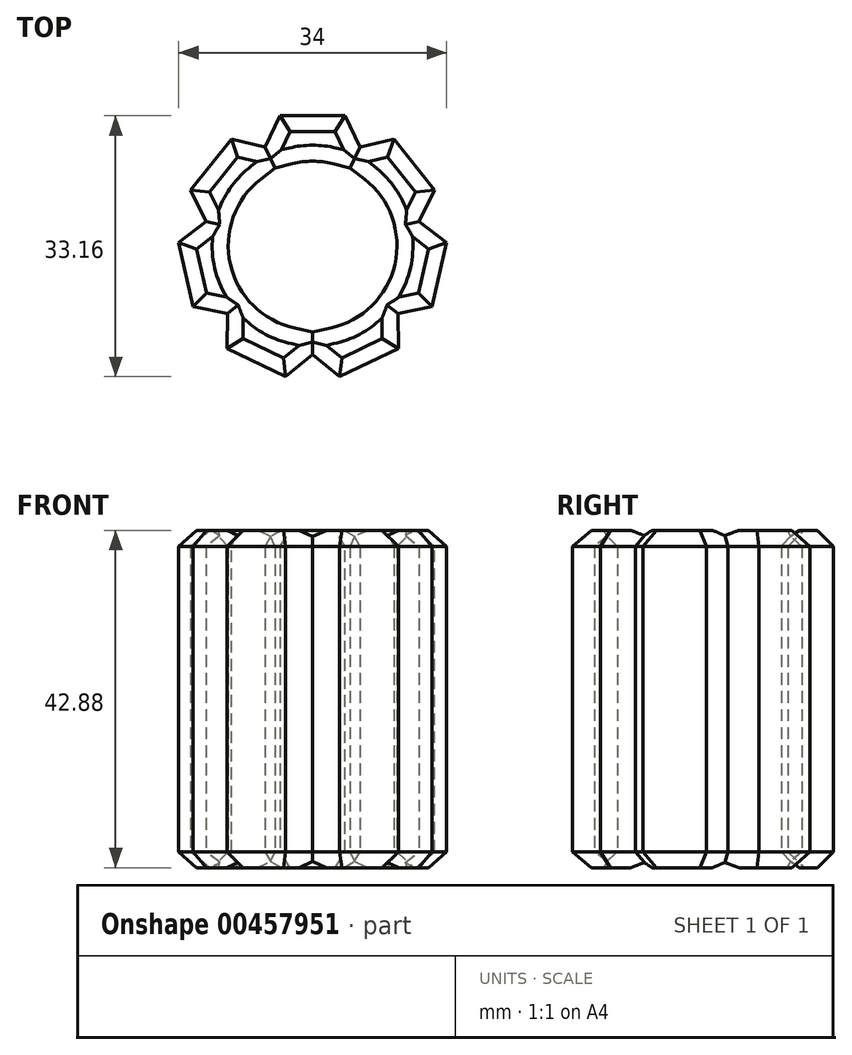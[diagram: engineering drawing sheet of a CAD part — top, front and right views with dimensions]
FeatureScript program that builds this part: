
annotation { "Feature Type Name" : "Feature", "Feature Type Description" : "" }
export const myFeature = defineFeature(function(context is Context, id is Id, definition is map)
    precondition{}
    {
        {
            var Q0;
            Q0=qCreatedBy(makeId("Top.planeOp"),FACE);
            var sketch = newSketch(context, id + "F0", { "sketchPlane" : qUnion([Q0])});
            skCircle(sketch, "E0", {"center": v(0, 0) * mm, "radius": 10.72 * mm});
            skLineSegment(sketch, "E1", {"start": v(0, 0) * mm, "end": v(0, 25.4) * mm, "construction": true});
            skPoint(sketch, "E2.center", {"position": v(-0.83, 0) * mm});
            skLineSegment(sketch, "E3", {"start": v(0, 25.4) * mm, "end": v(-11.82, 0) * mm});
            skLineSegment(sketch, "E4", {"start": v(0, 25.4) * mm, "end": v(11.82, 0) * mm});
            skLineSegment(sketch, "E5.1.0", {"start": v(-19.86, 15.84) * mm, "end": v(7.37, 9.24) * mm});
            skLineSegment(sketch, "E5.1.1", {"start": v(-19.86, 15.84) * mm, "end": v(-7.37, -9.24) * mm});
            skLineSegment(sketch, "E5.2.0", {"start": v(-24.76, -5.65) * mm, "end": v(-2.63, 11.53) * mm});
            skLineSegment(sketch, "E5.2.1", {"start": v(-24.76, -5.65) * mm, "end": v(2.63, -11.53) * mm});
            skLineSegment(sketch, "E5.3.0", {"start": v(-11.02, -22.88) * mm, "end": v(-10.65, 5.13) * mm});
            skLineSegment(sketch, "E5.3.1", {"start": v(-11.02, -22.88) * mm, "end": v(10.65, -5.13) * mm});
            skCircle(sketch, "E6", {"center": v(0, 0) * mm, "radius": 25.4 * mm});
            skLineSegment(sketch, "E7.2.4.0", {"start": v(11.02, -22.88) * mm, "end": v(-10.65, -5.13) * mm});
            skLineSegment(sketch, "E7.3.4.0", {"start": v(11.02, -22.88) * mm, "end": v(10.65, 5.13) * mm});
            skLineSegment(sketch, "E7.2.5.0", {"start": v(24.76, -5.65) * mm, "end": v(-2.63, -11.53) * mm});
            skLineSegment(sketch, "E7.3.5.0", {"start": v(24.76, -5.65) * mm, "end": v(2.63, 11.53) * mm});
            skLineSegment(sketch, "E7.2.6.0", {"start": v(19.86, 15.84) * mm, "end": v(7.37, -9.24) * mm});
            skLineSegment(sketch, "E7.3.6.0", {"start": v(19.86, 15.84) * mm, "end": v(-7.37, 9.24) * mm});
            skSolve(sketch);
        }
        {
            var Q0;
            {var subQ1=sQuery(id+"F0.wireOp",EDGE,"E3");var subQ7=sQuery(id+"F0.wireOp",EDGE,"E4");var subQ8=makeQuery(id+"F0.imprint","INTERSECT",VERTEX,{"derivedFrom":[subQ1,subQ7]});Q0=makeQuery(id+"F0.imprint","IMPRINT",FACE,{"disambiguationData":[TD([[makeQuery(id+"F0.imprint","IMPRINT",EDGE,{"disambiguationData":[TD([[subQ8,-1.0]])],"derivedFrom":subQ1}),1.0]])]});}
            var Q1;
            {var subQ1=sQuery(id+"F0.wireOp",EDGE,"E5.1.0");var subQ5=sQuery(id+"F0.wireOp",EDGE,"E3");var subQ10=makeQuery(id+"F0.imprint","INTERSECT",VERTEX,{"derivedFrom":[subQ5,subQ1]});Q1=makeQuery(id+"F0.imprint","IMPRINT",FACE,{"disambiguationData":[TD([[makeQuery(id+"F0.imprint","IMPRINT",EDGE,{"disambiguationData":[TD([[subQ10,-1.0]])],"derivedFrom":subQ5}),-1.0]])]});}
            var Q2;
            {var subQ1=sQuery(id+"F0.wireOp",EDGE,"E4");var subQ8=sQuery(id+"F0.wireOp",EDGE,"E5.3.1");var subQ9=makeQuery(id+"F0.imprint","INTERSECT",VERTEX,{"derivedFrom":[subQ1,subQ8]});Q2=makeQuery(id+"F0.imprint","IMPRINT",FACE,{"disambiguationData":[TD([[makeQuery(id+"F0.imprint","IMPRINT",EDGE,{"disambiguationData":[TD([[subQ9,-1.0]])],"derivedFrom":subQ1}),1.0]])]});}
            var Q3;
            {var subQ1=sQuery(id+"F0.wireOp",EDGE,"E5.2.0");var subQ3=sQuery(id+"F0.wireOp",EDGE,"E5.1.1");var subQ4=makeQuery(id+"F0.imprint","INTERSECT",VERTEX,{"derivedFrom":[subQ3,subQ1]});Q3=makeQuery(id+"F0.imprint","IMPRINT",FACE,{"disambiguationData":[TD([[makeQuery(id+"F0.imprint","IMPRINT",EDGE,{"disambiguationData":[TD([[subQ4,-1.0]])],"derivedFrom":subQ3}),-1.0]])]});}
            var Q4;
            {var subQ0=sQuery(id+"F0.wireOp",EDGE,"E5.3.0");var subQ1=sQuery(id+"F0.wireOp",EDGE,"E0");var subQ2=makeQuery(id+"F0.imprint","INTERSECT",VERTEX,{"derivedFrom":[subQ1,subQ0]});Q4=makeQuery(id+"F0.imprint","IMPRINT",FACE,{"disambiguationData":[TD([[makeQuery(id+"F0.imprint","IMPRINT",EDGE,{"disambiguationData":[TD([[subQ2,-1.0]])],"derivedFrom":subQ1}),-1.0]])]});}
            var Q5;
            {var subQ0=sQuery(id+"F0.wireOp",EDGE,"E5.2.0");var subQ1=sQuery(id+"F0.wireOp",EDGE,"E0");var subQ2=makeQuery(id+"F0.imprint","INTERSECT",VERTEX,{"derivedFrom":[subQ1,subQ0]});Q5=makeQuery(id+"F0.imprint","IMPRINT",FACE,{"disambiguationData":[TD([[makeQuery(id+"F0.imprint","IMPRINT",EDGE,{"disambiguationData":[TD([[subQ2,-1.0]])],"derivedFrom":subQ1}),-1.0]])]});}
            var Q6;
            {var subQ0=sQuery(id+"F0.wireOp",EDGE,"E5.1.0");var subQ1=sQuery(id+"F0.wireOp",EDGE,"E0");var subQ2=makeQuery(id+"F0.imprint","INTERSECT",VERTEX,{"derivedFrom":[subQ1,subQ0]});Q6=makeQuery(id+"F0.imprint","IMPRINT",FACE,{"disambiguationData":[TD([[makeQuery(id+"F0.imprint","IMPRINT",EDGE,{"disambiguationData":[TD([[subQ2,-1.0]])],"derivedFrom":subQ1}),-1.0]])]});}
            var Q7;
            {var subQ0=sQuery(id+"F0.wireOp",EDGE,"E5.3.1");var subQ1=sQuery(id+"F0.wireOp",EDGE,"E0");var subQ2=makeQuery(id+"F0.imprint","INTERSECT",VERTEX,{"derivedFrom":[subQ1,subQ0]});Q7=makeQuery(id+"F0.imprint","IMPRINT",FACE,{"disambiguationData":[TD([[makeQuery(id+"F0.imprint","IMPRINT",EDGE,{"disambiguationData":[TD([[subQ2,1.0]])],"derivedFrom":subQ1}),-1.0]])]});}
            var Q8;
            {var subQ0=sQuery(id+"F0.wireOp",EDGE,"E4");var subQ1=sQuery(id+"F0.wireOp",EDGE,"E0");var subQ2=makeQuery(id+"F0.imprint","INTERSECT",VERTEX,{"derivedFrom":[subQ1,subQ0]});Q8=makeQuery(id+"F0.imprint","IMPRINT",FACE,{"disambiguationData":[TD([[makeQuery(id+"F0.imprint","IMPRINT",EDGE,{"disambiguationData":[TD([[subQ2,1.0]])],"derivedFrom":subQ1}),-1.0]])]});}
            var Q9;
            {var subQ0=sQuery(id+"F0.wireOp",EDGE,"E5.1.1");var subQ1=sQuery(id+"F0.wireOp",EDGE,"E0");var subQ2=makeQuery(id+"F0.imprint","INTERSECT",VERTEX,{"derivedFrom":[subQ1,subQ0]});Q9=makeQuery(id+"F0.imprint","IMPRINT",FACE,{"disambiguationData":[TD([[makeQuery(id+"F0.imprint","IMPRINT",EDGE,{"disambiguationData":[TD([[subQ2,-1.0]])],"derivedFrom":subQ1}),-1.0]])]});}
            var Q10;
            {var subQ0=sQuery(id+"F0.wireOp",EDGE,"E3");var subQ1=sQuery(id+"F0.wireOp",EDGE,"E0");var subQ2=makeQuery(id+"F0.imprint","INTERSECT",VERTEX,{"derivedFrom":[subQ1,subQ0]});Q10=makeQuery(id+"F0.imprint","IMPRINT",FACE,{"disambiguationData":[TD([[makeQuery(id+"F0.imprint","IMPRINT",EDGE,{"disambiguationData":[TD([[subQ2,-1.0]])],"derivedFrom":subQ1}),-1.0]])]});}
            var Q11;
            {var subQ0=sQuery(id+"F0.wireOp",EDGE,"E5.3.1");var subQ1=sQuery(id+"F0.wireOp",EDGE,"E0");var subQ2=makeQuery(id+"F0.imprint","INTERSECT",VERTEX,{"derivedFrom":[subQ1,subQ0]});Q11=makeQuery(id+"F0.imprint","IMPRINT",FACE,{"disambiguationData":[TD([[makeQuery(id+"F0.imprint","IMPRINT",EDGE,{"disambiguationData":[TD([[subQ2,-1.0]])],"derivedFrom":subQ1}),-1.0]])]});}
            var Q12;
            {var subQ0=sQuery(id+"F0.wireOp",EDGE,"E7.2.5.0");var subQ1=sQuery(id+"F0.wireOp",EDGE,"E7.3.4.0");var subQ2=makeQuery(id+"F0.imprint","INTERSECT",VERTEX,{"derivedFrom":[subQ1,subQ0]});Q12=makeQuery(id+"F0.imprint","IMPRINT",FACE,{"disambiguationData":[TD([[makeQuery(id+"F0.imprint","IMPRINT",EDGE,{"disambiguationData":[TD([[subQ2,-1.0]])],"derivedFrom":subQ1}),-1.0]])]});}
            var Q13;
            {var subQ0=sQuery(id+"F0.wireOp",EDGE,"E7.2.4.0");var subQ1=sQuery(id+"F0.wireOp",EDGE,"E5.3.1");var subQ2=makeQuery(id+"F0.imprint","INTERSECT",VERTEX,{"derivedFrom":[subQ1,subQ0]});Q13=makeQuery(id+"F0.imprint","IMPRINT",FACE,{"disambiguationData":[TD([[makeQuery(id+"F0.imprint","IMPRINT",EDGE,{"disambiguationData":[TD([[subQ2,-1.0]])],"derivedFrom":subQ1}),-1.0]])]});}
            var Q14;
            {var subQ0=sQuery(id+"F0.wireOp",EDGE,"E5.3.0");var subQ1=sQuery(id+"F0.wireOp",EDGE,"E5.2.1");var subQ2=makeQuery(id+"F0.imprint","INTERSECT",VERTEX,{"derivedFrom":[subQ1,subQ0]});Q14=makeQuery(id+"F0.imprint","IMPRINT",FACE,{"disambiguationData":[TD([[makeQuery(id+"F0.imprint","IMPRINT",EDGE,{"disambiguationData":[TD([[subQ2,-1.0]])],"derivedFrom":subQ1}),-1.0]])]});}
            var Q15;
            {var subQ0=sQuery(id+"F0.wireOp",EDGE,"E7.3.6.0");var subQ1=sQuery(id+"F0.wireOp",EDGE,"E4");var subQ2=makeQuery(id+"F0.imprint","INTERSECT",VERTEX,{"derivedFrom":[subQ1,subQ0]});Q15=makeQuery(id+"F0.imprint","IMPRINT",FACE,{"disambiguationData":[TD([[makeQuery(id+"F0.imprint","IMPRINT",EDGE,{"disambiguationData":[TD([[subQ2,-1.0]])],"derivedFrom":subQ1}),1.0]])]});}
            var Q16;
            {var subQ3=sQuery(id+"F0.wireOp",EDGE,"E4");var subQ8=sQuery(id+"F0.wireOp",EDGE,"E7.3.6.0");var subQ10=makeQuery(id+"F0.imprint","INTERSECT",VERTEX,{"derivedFrom":[subQ3,subQ8]});Q16=makeQuery(id+"F0.imprint","IMPRINT",FACE,{"disambiguationData":[TD([[makeQuery(id+"F0.imprint","IMPRINT",EDGE,{"disambiguationData":[TD([[subQ10,-1.0]])],"derivedFrom":subQ3}),-1.0]])]});}
            var Q17;
            {var subQ1=sQuery(id+"F0.wireOp",EDGE,"E5.3.1");var subQ8=sQuery(id+"F0.wireOp",EDGE,"E0");var subQ9=makeQuery(id+"F0.imprint","INTERSECT",VERTEX,{"derivedFrom":[subQ8,subQ1]});Q17=makeQuery(id+"F0.imprint","IMPRINT",FACE,{"disambiguationData":[TD([[makeQuery(id+"F0.imprint","IMPRINT",EDGE,{"disambiguationData":[TD([[subQ9,1.0]])],"derivedFrom":subQ1}),-1.0]])]});}
            var Q18;
            {var subQ1=sQuery(id+"F0.wireOp",EDGE,"E5.2.1");var subQ8=sQuery(id+"F0.wireOp",EDGE,"E0");var subQ9=makeQuery(id+"F0.imprint","INTERSECT",VERTEX,{"derivedFrom":[subQ8,subQ1]});Q18=makeQuery(id+"F0.imprint","IMPRINT",FACE,{"disambiguationData":[TD([[makeQuery(id+"F0.imprint","IMPRINT",EDGE,{"disambiguationData":[TD([[subQ9,1.0]])],"derivedFrom":subQ1}),-1.0]])]});}
            var Q19;
            {var subQ0=sQuery(id+"F0.wireOp",EDGE,"E4");var subQ1=sQuery(id+"F0.wireOp",EDGE,"E0");var subQ2=makeQuery(id+"F0.imprint","INTERSECT",VERTEX,{"derivedFrom":[subQ1,subQ0]});Q19=makeQuery(id+"F0.imprint","IMPRINT",FACE,{"disambiguationData":[TD([[makeQuery(id+"F0.imprint","IMPRINT",EDGE,{"disambiguationData":[TD([[subQ2,-1.0]])],"derivedFrom":subQ1}),-1.0]])]});}
            var Q20;
            {var subQ0=sQuery(id+"F0.wireOp",EDGE,"E7.3.4.0");var subQ1=sQuery(id+"F0.wireOp",EDGE,"E0");var subQ2=makeQuery(id+"F0.imprint","INTERSECT",VERTEX,{"derivedFrom":[subQ1,subQ0]});Q20=makeQuery(id+"F0.imprint","IMPRINT",FACE,{"disambiguationData":[TD([[makeQuery(id+"F0.imprint","IMPRINT",EDGE,{"disambiguationData":[TD([[subQ2,1.0]])],"derivedFrom":subQ1}),-1.0]])]});}
            var Q21;
            {var subQ3=sQuery(id+"F0.wireOp",EDGE,"E3");var subQ8=sQuery(id+"F0.wireOp",EDGE,"E5.1.0");var subQ9=makeQuery(id+"F0.imprint","INTERSECT",VERTEX,{"derivedFrom":[subQ3,subQ8]});Q21=makeQuery(id+"F0.imprint","IMPRINT",FACE,{"disambiguationData":[TD([[makeQuery(id+"F0.imprint","IMPRINT",EDGE,{"disambiguationData":[TD([[subQ9,-1.0]])],"derivedFrom":subQ3}),1.0]])]});}
            var Q22;
            {var subQ5=sQuery(id+"F0.wireOp",EDGE,"E3");var subQ6=sQuery(id+"F0.wireOp",EDGE,"E0");var subQ7=makeQuery(id+"F0.imprint","INTERSECT",VERTEX,{"derivedFrom":[subQ6,subQ5]});Q22=makeQuery(id+"F0.imprint","IMPRINT",FACE,{"disambiguationData":[TD([[makeQuery(id+"F0.imprint","IMPRINT",EDGE,{"disambiguationData":[TD([[subQ7,1.0]])],"derivedFrom":subQ5}),-1.0]])]});}
            var Q23;
            {var subQ5=sQuery(id+"F0.wireOp",EDGE,"E5.1.1");var subQ7=sQuery(id+"F0.wireOp",EDGE,"E0");var subQ8=makeQuery(id+"F0.imprint","INTERSECT",VERTEX,{"derivedFrom":[subQ7,subQ5]});Q23=makeQuery(id+"F0.imprint","IMPRINT",FACE,{"disambiguationData":[TD([[makeQuery(id+"F0.imprint","IMPRINT",EDGE,{"disambiguationData":[TD([[subQ8,1.0]])],"derivedFrom":subQ5}),-1.0]])]});}
            var Q24;
            {var subQ0=sQuery(id+"F0.wireOp",EDGE,"E7.2.4.0");var subQ1=sQuery(id+"F0.wireOp",EDGE,"E0");var subQ2=makeQuery(id+"F0.imprint","INTERSECT",VERTEX,{"derivedFrom":[subQ1,subQ0]});Q24=makeQuery(id+"F0.imprint","IMPRINT",FACE,{"disambiguationData":[TD([[makeQuery(id+"F0.imprint","IMPRINT",EDGE,{"disambiguationData":[TD([[subQ2,-1.0]])],"derivedFrom":subQ1}),-1.0]])]});}
            extrude(context, id + "F1", {"entities" : qUnion([Q0, Q1, Q2, Q3, Q4, Q5, Q6, Q7, Q8, Q9, Q10, Q11, Q12, Q13, Q14, Q15, Q16, Q17, Q18, Q19, Q20, Q21, Q22, Q23, Q24]), "endBound" : BoundingType.SYMMETRIC, "depth" : 42.88 * mm, "offsetDistance" : 25.4 * mm});
        }
        {
            var Q0;
            Q0=makeQuery(id+"F1.opExtrude","SWEPT_EDGE",EDGE,{"disambiguationData":[OSD([sQuery(id+"F0.wireOp",EDGE,"E6"),sQuery(id+"F0.wireOp",EDGE,"E7.2.5.0"),sQuery(id+"F0.wireOp",EDGE,"E7.3.5.0")])]});
            var Q1;
            Q1=makeQuery(id+"F1.opExtrude","SWEPT_EDGE",EDGE,{"disambiguationData":[OSD([sQuery(id+"F0.wireOp",EDGE,"E6"),sQuery(id+"F0.wireOp",EDGE,"E7.2.6.0"),sQuery(id+"F0.wireOp",EDGE,"E7.3.6.0")])]});
            var Q2;
            Q2=makeQuery(id+"F1.opExtrude","SWEPT_EDGE",EDGE,{"disambiguationData":[OSD([sQuery(id+"F0.wireOp",EDGE,"E5.1.0"),sQuery(id+"F0.wireOp",EDGE,"E5.1.1"),sQuery(id+"F0.wireOp",EDGE,"E6")])]});
            var Q3;
            Q3=makeQuery(id+"F1.opExtrude","SWEPT_EDGE",EDGE,{"disambiguationData":[OSD([sQuery(id+"F0.wireOp",EDGE,"E5.2.0"),sQuery(id+"F0.wireOp",EDGE,"E5.2.1"),sQuery(id+"F0.wireOp",EDGE,"E6")])]});
            var Q4;
            Q4=makeQuery(id+"F1.opExtrude","SWEPT_EDGE",EDGE,{"disambiguationData":[OSD([sQuery(id+"F0.wireOp",EDGE,"E5.3.0"),sQuery(id+"F0.wireOp",EDGE,"E5.3.1"),sQuery(id+"F0.wireOp",EDGE,"E6")])]});
            var Q5;
            Q5=makeQuery(id+"F1.opExtrude","SWEPT_EDGE",EDGE,{"disambiguationData":[OSD([sQuery(id+"F0.wireOp",EDGE,"E6"),sQuery(id+"F0.wireOp",EDGE,"E7.2.4.0"),sQuery(id+"F0.wireOp",EDGE,"E7.3.4.0")])]});
            var Q6;
            Q6=makeQuery(id+"F1.opExtrude","SWEPT_EDGE",EDGE,{"disambiguationData":[OSD([sQuery(id+"F0.wireOp",EDGE,"E3"),sQuery(id+"F0.wireOp",EDGE,"E4"),sQuery(id+"F0.wireOp",EDGE,"E6")])]});
            chamfer(context, id + "F2", {"entities" : qUnion([Q0, Q1, Q2, Q3, Q4, Q5, Q6]), "width" : 4.57 * mm, "tangentPropagation" : true});
        }
        {
            var Q0;
            Q0=makeQuery(id+"F1.opExtrude","CAP_FACE",FACE,{"disambiguationData":[OSD([sQuery(id+"F0.wireOp",EDGE,"E0"),sQuery(id+"F0.wireOp",EDGE,"xcRdsuIS-1Vm6-WT5r-Rajy-LAlO8bjhWdF4"),sQuery(id+"F0.wireOp",EDGE,"muXb6j68-2s0r-oRPZ-5IFS-jHZvXMtzUGro"),sQuery(id+"F0.wireOp",EDGE,"E2.1.0"),sQuery(id+"F0.wireOp",EDGE,"E2.1.1"),sQuery(id+"F0.wireOp",EDGE,"E2.2.0"),sQuery(id+"F0.wireOp",EDGE,"E2.2.1"),sQuery(id+"F0.wireOp",EDGE,"E2.3.0"),sQuery(id+"F0.wireOp",EDGE,"E2.3.1")])],"isStart":false});
            var Q1;
            Q1=makeQuery(id+"F1.opExtrude","CAP_FACE",FACE,{"disambiguationData":[OSD([sQuery(id+"F0.wireOp",EDGE,"E0"),sQuery(id+"F0.wireOp",EDGE,"xcRdsuIS-1Vm6-WT5r-Rajy-LAlO8bjhWdF4"),sQuery(id+"F0.wireOp",EDGE,"muXb6j68-2s0r-oRPZ-5IFS-jHZvXMtzUGro"),sQuery(id+"F0.wireOp",EDGE,"E2.1.0"),sQuery(id+"F0.wireOp",EDGE,"E2.1.1"),sQuery(id+"F0.wireOp",EDGE,"E2.2.0"),sQuery(id+"F0.wireOp",EDGE,"E2.2.1"),sQuery(id+"F0.wireOp",EDGE,"E2.3.0"),sQuery(id+"F0.wireOp",EDGE,"E2.3.1")])],"isStart":true});
            chamfer(context, id + "F3", {"entities" : qUnion([Q0, Q1]), "width" : 2.03 * mm, "tangentPropagation" : true});
        }
    });
